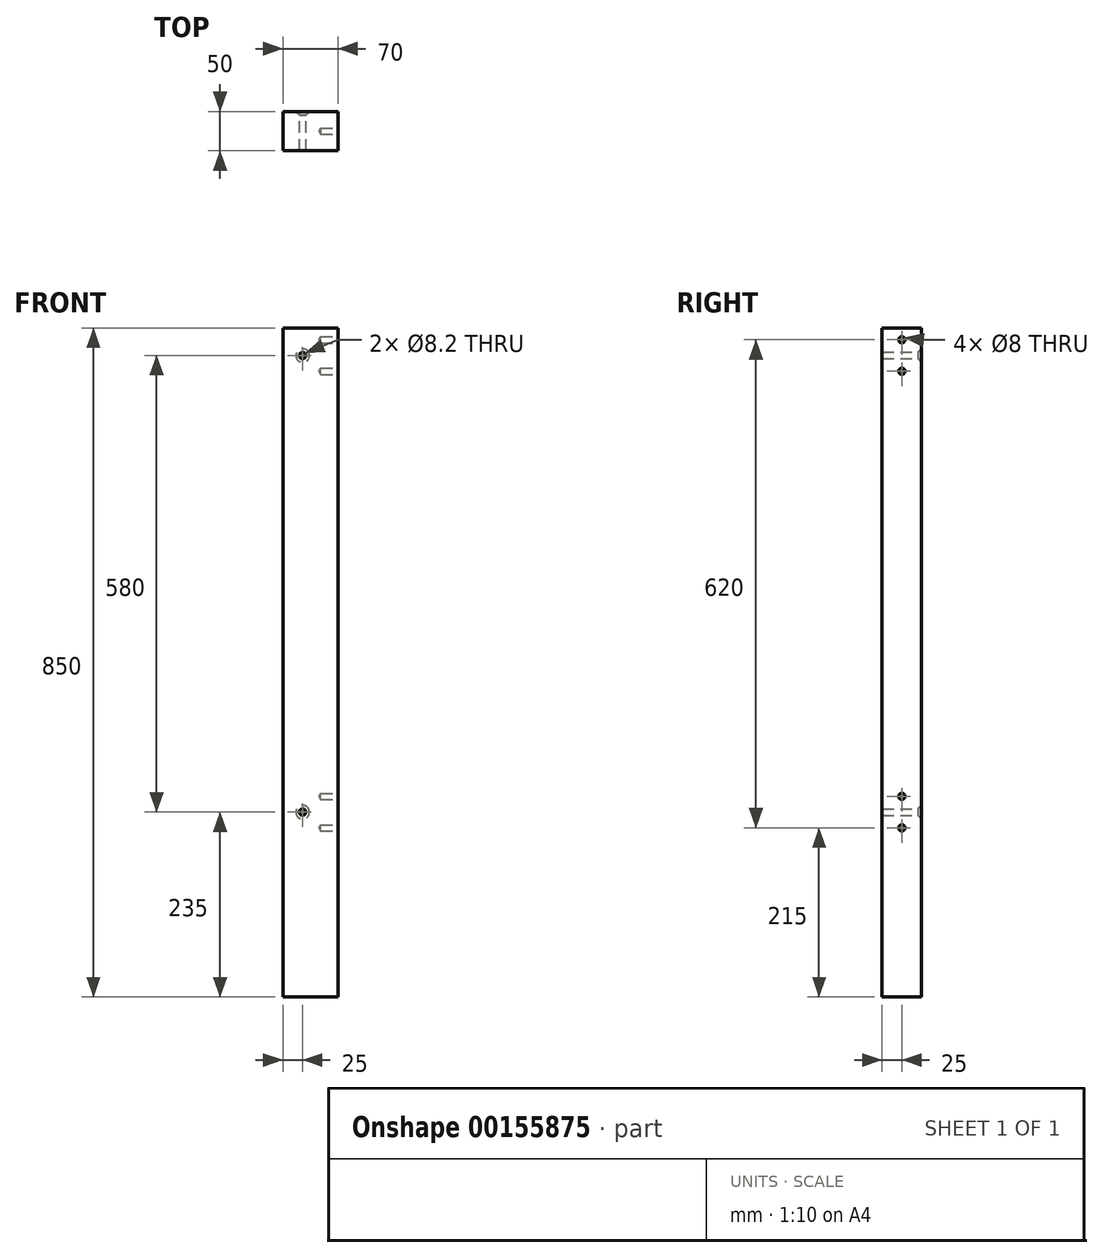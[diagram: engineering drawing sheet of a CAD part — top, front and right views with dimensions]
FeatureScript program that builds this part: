
annotation { "Feature Type Name" : "Feature", "Feature Type Description" : "" }
export const myFeature = defineFeature(function(context is Context, id is Id, definition is map)
    precondition{}
    {
        {
            var Q0;
            Q0=qCreatedBy(makeId("Top.planeOp"),FACE);
            var sketch = newSketch(context, id + "F0", { "sketchPlane" : qUnion([Q0])});
            skLineSegment(sketch, "E0.bottom", {"start": v(35, 25) * mm, "end": v(-35, 25) * mm});
            skLineSegment(sketch, "E0.top", {"start": v(35, -25) * mm, "end": v(-35, -25) * mm});
            skLineSegment(sketch, "E0.left", {"start": v(35, 25) * mm, "end": v(35, -25) * mm});
            skLineSegment(sketch, "E0.right", {"start": v(-35, 25) * mm, "end": v(-35, -25) * mm});
            skPoint(sketch, "E0.middle", {"position": v(0, 0) * mm});
            skSolve(sketch);
        }
        {
            var Q0;
            Q0=makeQuery(id+"F0.imprint","IMPRINT",FACE,{"disambiguationData":[TD([[makeQuery(id+"F0.imprint","IMPRINT",EDGE,{"derivedFrom":sQuery(id+"F0.wireOp",EDGE,"E0.bottom")}),1.0]])]});
            extrude(context, id + "F1", {"entities" : qUnion([Q0]), "depth" : 850 * mm});
        }
        {
            var Q0;
            Q0=makeQuery(id+"F1.opExtrude","SWEPT_FACE",FACE,{"disambiguationData":[OSD([sQuery(id+"F0.wireOp",EDGE,"E0.left")])]});
            var sketch = newSketch(context, id + "F2", { "sketchPlane" : qUnion([Q0])});
            skPoint(sketch, "E1", {"position": v(0, 215) * mm});
            skPoint(sketch, "E2", {"position": v(0, 255) * mm});
            skPoint(sketch, "E3", {"position": v(0, 795) * mm});
            skPoint(sketch, "E4", {"position": v(0, 835) * mm});
            skSolve(sketch);
        }
        {
            var Q0;
            Q0=sQuery(id+"F2.wireOp",VERTEX,"E1");
            var Q1;
            Q1=sQuery(id+"F2.wireOp",VERTEX,"E2");
            var Q2;
            Q2=sQuery(id+"F2.wireOp",VERTEX,"E3");
            var Q3;
            Q3=sQuery(id+"F2.wireOp",VERTEX,"E4");
            var Q4;
            Q4=makeQuery(id+"F1.opExtrude","SWEPT_BODY",BODY,{"disambiguationData":[OSD([sQuery(id+"F0.wireOp",EDGE,"E0.bottom"),sQuery(id+"F0.wireOp",EDGE,"E0.top"),sQuery(id+"F0.wireOp",EDGE,"E0.left"),sQuery(id+"F0.wireOp",EDGE,"E0.right")])]});
            hole(context, id + "F3", {"style" : HoleStyle.SIMPLE, "endStyle" : HoleEndStyle.BLIND, "holeDiameter" : 8 * mm, "holeDepth" : 22 * mm, "locations" : qUnion([Q0, Q1, Q2, Q3]), "scope" : qUnion([Q4])});
        }
        {
            var Q0;
            Q0=makeQuery(id+"F1.opExtrude","SWEPT_FACE",FACE,{"disambiguationData":[OSD([sQuery(id+"F0.wireOp",EDGE,"E0.bottom")])]});
            var sketch = newSketch(context, id + "F4", { "sketchPlane" : qUnion([Q0])});
            skPoint(sketch, "E5", {"position": v(10, 235) * mm});
            skPoint(sketch, "E6", {"position": v(10, 815) * mm});
            skSolve(sketch);
        }
        {
            var Q0;
            Q0=sQuery(id+"F4.wireOp",VERTEX,"E5");
            var Q1;
            Q1=sQuery(id+"F4.wireOp",VERTEX,"E6");
            var Q2;
            Q2=makeQuery(id+"F1.opExtrude","SWEPT_BODY",BODY,{"disambiguationData":[OSD([sQuery(id+"F0.wireOp",EDGE,"E0.bottom"),sQuery(id+"F0.wireOp",EDGE,"E0.top"),sQuery(id+"F0.wireOp",EDGE,"E0.left"),sQuery(id+"F0.wireOp",EDGE,"E0.right")])]});
            hole(context, id + "F5", {"style" : HoleStyle.C_SINK, "endStyle" : HoleEndStyle.THROUGH, "holeDiameter" : 8.2 * mm, "cSinkDiameter" : 17.3 * mm, "cSinkAngle" : 90 * degree, "locations" : qUnion([Q0, Q1]), "scope" : qUnion([Q2]), "isTappedThrough" : true});
        }
    });
